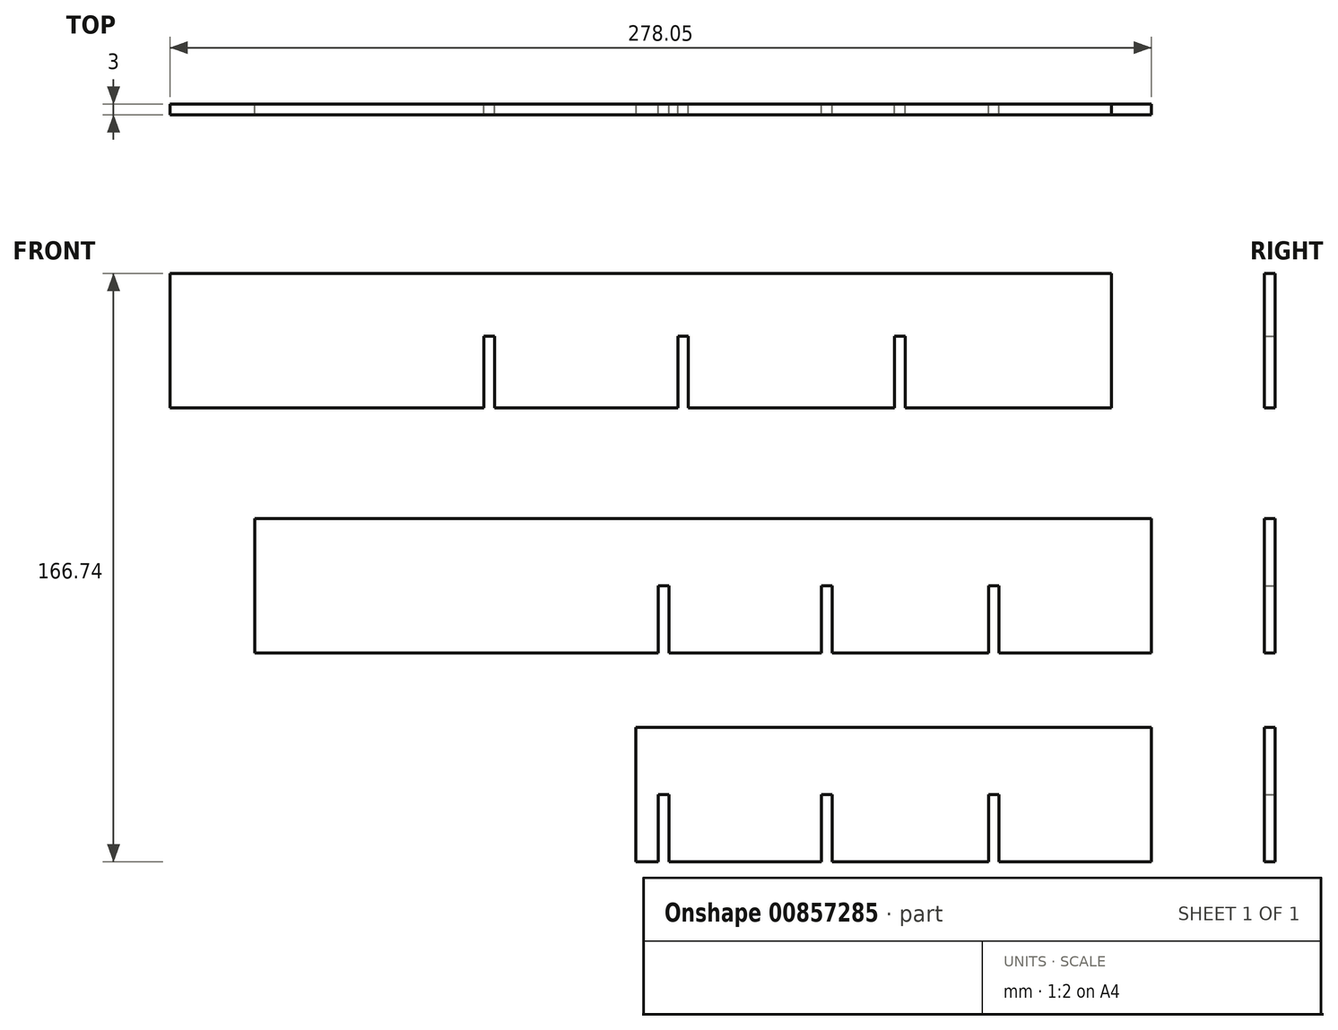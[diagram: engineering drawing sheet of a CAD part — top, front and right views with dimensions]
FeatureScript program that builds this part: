
annotation { "Feature Type Name" : "Feature", "Feature Type Description" : "" }
export const myFeature = defineFeature(function(context is Context, id is Id, definition is map)
    precondition{}
    {
        {
            var Q0;
            Q0=qCreatedBy(makeId("Front.planeOp"),FACE);
            var sketch = newSketch(context, id + "F0", { "sketchPlane" : qUnion([Q0])});
            skLineSegment(sketch, "E0.bottom", {"start": v(0, 0) * mm, "end": v(-266.7, 0) * mm});
            skLineSegment(sketch, "E0.top", {"start": v(0, 38.1) * mm, "end": v(-266.7, 38.1) * mm});
            skLineSegment(sketch, "E0.left", {"start": v(0, 0) * mm, "end": v(0, 38.1) * mm});
            skLineSegment(sketch, "E0.right", {"start": v(-266.7, 0) * mm, "end": v(-266.7, 38.1) * mm});
            skLineSegment(sketch, "E1.bottom", {"start": v(-177.8, 0) * mm, "end": v(-174.8, 0) * mm});
            skLineSegment(sketch, "E1.top", {"start": v(-177.8, 20.32) * mm, "end": v(-174.8, 20.32) * mm});
            skLineSegment(sketch, "E1.left", {"start": v(-177.8, 0) * mm, "end": v(-177.8, 20.32) * mm});
            skLineSegment(sketch, "E1.right", {"start": v(-174.8, 0) * mm, "end": v(-174.8, 20.32) * mm});
            skLineSegment(sketch, "E2.bottom", {"start": v(-61.42, 0) * mm, "end": v(-58.42, 0) * mm});
            skLineSegment(sketch, "E2.top", {"start": v(-61.42, 20.32) * mm, "end": v(-58.42, 20.32) * mm});
            skLineSegment(sketch, "E2.left", {"start": v(-61.42, 0) * mm, "end": v(-61.42, 20.32) * mm});
            skLineSegment(sketch, "E2.right", {"start": v(-58.42, 0) * mm, "end": v(-58.42, 20.32) * mm});
            skLineSegment(sketch, "E3.bottom", {"start": v(-122.84, 0) * mm, "end": v(-119.84, 0) * mm});
            skLineSegment(sketch, "E3.top", {"start": v(-122.84, 20.32) * mm, "end": v(-119.84, 20.32) * mm});
            skLineSegment(sketch, "E3.left", {"start": v(-122.84, 0) * mm, "end": v(-122.84, 20.32) * mm});
            skLineSegment(sketch, "E3.right", {"start": v(-119.84, 0) * mm, "end": v(-119.84, 20.32) * mm});
            skSolve(sketch);
        }
        {
            var Q0;
            Q0=makeQuery(id+"F0.imprint","IMPRINT",FACE,{"disambiguationData":[TD([[makeQuery(id+"F0.imprint","IMPRINT",EDGE,{"derivedFrom":sQuery(id+"F0.wireOp",EDGE,"E0.top")}),1.0]])]});
            extrude(context, id + "F1", {"entities" : qUnion([Q0]), "depth" : 3 * mm, "offsetDistance" : 25.4 * mm});
        }
        {
            var Q0;
            Q0=qCreatedBy(makeId("Front.planeOp"),FACE);
            var sketch = newSketch(context, id + "F2", { "sketchPlane" : qUnion([Q0])});
            skLineSegment(sketch, "E4.bottom", {"start": v(-242.65, -31.36) * mm, "end": v(11.35, -31.36) * mm});
            skLineSegment(sketch, "E4.top", {"start": v(-242.65, -69.46) * mm, "end": v(11.35, -69.46) * mm});
            skLineSegment(sketch, "E4.left", {"start": v(-242.65, -31.36) * mm, "end": v(-242.65, -69.46) * mm});
            skLineSegment(sketch, "E4.right", {"start": v(11.35, -31.36) * mm, "end": v(11.35, -69.46) * mm});
            skLineSegment(sketch, "E5.bottom", {"start": v(-128.35, -69.46) * mm, "end": v(-125.35, -69.46) * mm});
            skLineSegment(sketch, "E5.top", {"start": v(-128.35, -50.41) * mm, "end": v(-125.35, -50.41) * mm});
            skLineSegment(sketch, "E5.left", {"start": v(-128.35, -69.46) * mm, "end": v(-128.35, -50.41) * mm});
            skLineSegment(sketch, "E5.right", {"start": v(-125.35, -69.46) * mm, "end": v(-125.35, -50.41) * mm});
            skLineSegment(sketch, "E6.bottom", {"start": v(-82.17, -69.46) * mm, "end": v(-79.17, -69.46) * mm});
            skLineSegment(sketch, "E6.top", {"start": v(-82.17, -50.41) * mm, "end": v(-79.17, -50.41) * mm});
            skLineSegment(sketch, "E6.left", {"start": v(-82.17, -69.46) * mm, "end": v(-82.17, -50.41) * mm});
            skLineSegment(sketch, "E6.right", {"start": v(-79.17, -69.46) * mm, "end": v(-79.17, -50.41) * mm});
            skLineSegment(sketch, "E7.bottom", {"start": v(-34.83, -69.46) * mm, "end": v(-31.83, -69.46) * mm});
            skLineSegment(sketch, "E7.top", {"start": v(-34.83, -50.41) * mm, "end": v(-31.83, -50.41) * mm});
            skLineSegment(sketch, "E7.left", {"start": v(-34.83, -69.46) * mm, "end": v(-34.83, -50.41) * mm});
            skLineSegment(sketch, "E7.right", {"start": v(-31.83, -69.46) * mm, "end": v(-31.83, -50.41) * mm});
            skSolve(sketch);
        }
        {
            var Q0;
            Q0=makeQuery(id+"F2.imprint","IMPRINT",FACE,{"disambiguationData":[TD([[makeQuery(id+"F2.imprint","IMPRINT",EDGE,{"derivedFrom":sQuery(id+"F2.wireOp",EDGE,"E4.bottom")}),-1.0]])]});
            extrude(context, id + "F3", {"entities" : qUnion([Q0]), "depth" : 3 * mm, "offsetDistance" : 25.4 * mm});
        }
        {
            var Q0;
            Q0=makeQuery(id+"F3.opExtrude","SWEPT_BODY",BODY,{"disambiguationData":[OSD([sQuery(id+"F2.wireOp",EDGE,"E4.bottom"),sQuery(id+"F2.wireOp",EDGE,"E4.top"),sQuery(id+"F2.wireOp",EDGE,"E4.left"),sQuery(id+"F2.wireOp",EDGE,"E4.right"),sQuery(id+"F2.wireOp",EDGE,"E5.top"),sQuery(id+"F2.wireOp",EDGE,"E5.left"),sQuery(id+"F2.wireOp",EDGE,"E5.right"),sQuery(id+"F2.wireOp",EDGE,"E6.top"),sQuery(id+"F2.wireOp",EDGE,"E6.left"),sQuery(id+"F2.wireOp",EDGE,"E6.right"),sQuery(id+"F2.wireOp",EDGE,"E7.top"),sQuery(id+"F2.wireOp",EDGE,"E7.left"),sQuery(id+"F2.wireOp",EDGE,"E7.right")])]});
            transform(context, id + "F4", {"entities" : qUnion([Q0]), "transformType" : TransformType.TRANSLATION_3D, "dx" : 0 * mm, "dy" : 0 * mm, "dz" : -59.18 * mm, "makeCopy" : true});
        }
        {
            var Q0;
            Q0=makeQuery(id+"F4.opPattern","COPY",FACE,{"derivedFrom":makeQuery(id+"F3.opExtrude","CAP_FACE",FACE,{"disambiguationData":[OSD([sQuery(id+"F2.wireOp",EDGE,"E4.bottom"),sQuery(id+"F2.wireOp",EDGE,"E4.top"),sQuery(id+"F2.wireOp",EDGE,"E4.left"),sQuery(id+"F2.wireOp",EDGE,"E4.right"),sQuery(id+"F2.wireOp",EDGE,"E5.top"),sQuery(id+"F2.wireOp",EDGE,"E5.left"),sQuery(id+"F2.wireOp",EDGE,"E5.right"),sQuery(id+"F2.wireOp",EDGE,"E6.top"),sQuery(id+"F2.wireOp",EDGE,"E6.left"),sQuery(id+"F2.wireOp",EDGE,"E6.right"),sQuery(id+"F2.wireOp",EDGE,"E7.top"),sQuery(id+"F2.wireOp",EDGE,"E7.left"),sQuery(id+"F2.wireOp",EDGE,"E7.right")])],"isStart":false}),"instanceName":"1"});
            var sketch = newSketch(context, id + "F5", { "sketchPlane" : qUnion([Q0])});
            skLineSegment(sketch, "E8", {"start": v(-134.7, -90.54) * mm, "end": v(-134.7, -128.64) * mm});
            skSolve(sketch);
        }
        {
            var Q0;
            {var subQ0=sQuery(id+"F5.wireOp",EDGE,"E8");Q0=makeQuery(id+"F5.imprint","IMPRINT",FACE,{"disambiguationData":[TD([[makeQuery(id+"F5.imprint","IMPRINT",EDGE,{"derivedFrom":subQ0}),-1.0]])]});}
            extrude(context, id + "F6", {"entities" : qUnion([Q0]), "operationType" : NewBodyOperationType.REMOVE, "oppositeDirection" : true, "depth" : 25.4 * mm, "offsetDistance" : 25.4 * mm});
        }
    });
